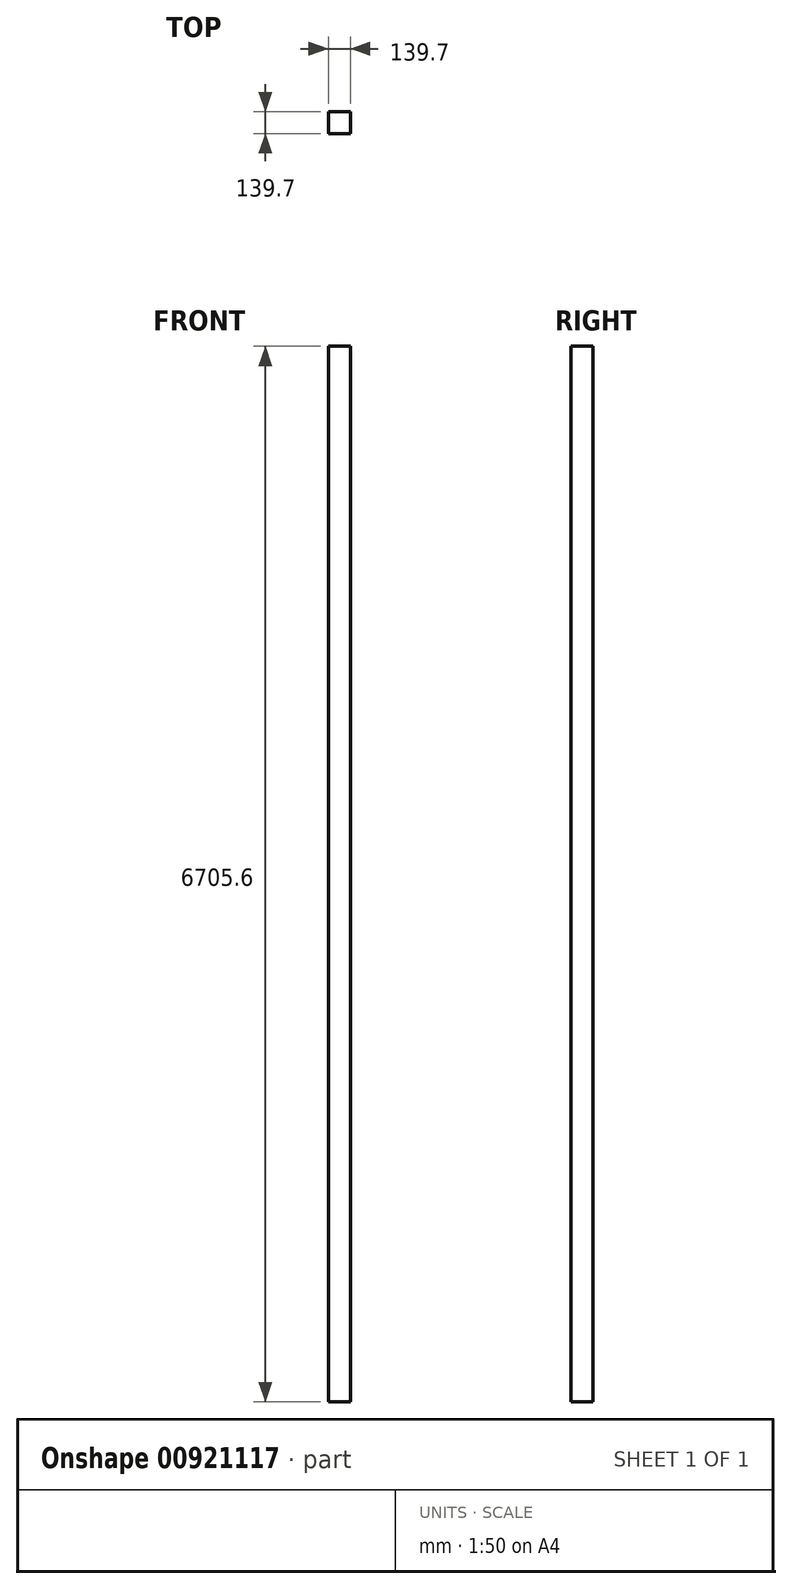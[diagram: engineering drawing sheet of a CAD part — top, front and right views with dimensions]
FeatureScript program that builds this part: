
annotation { "Feature Type Name" : "Feature", "Feature Type Description" : "" }
export const myFeature = defineFeature(function(context is Context, id is Id, definition is map)
    precondition{}
    {
        {
            var Q0;
            Q0=qCreatedBy(makeId("Top.planeOp"),FACE);
            var sketch = newSketch(context, id + "F0", { "sketchPlane" : qUnion([Q0])});
            skLineSegment(sketch, "E0.bottom", {"start": v(0, 40.07) * mm, "end": v(139.7, 40.07) * mm});
            skLineSegment(sketch, "E0.top", {"start": v(0, -99.63) * mm, "end": v(139.7, -99.63) * mm});
            skLineSegment(sketch, "E0.left", {"start": v(0, 40.07) * mm, "end": v(0, -99.63) * mm});
            skLineSegment(sketch, "E0.right", {"start": v(139.7, 40.07) * mm, "end": v(139.7, -99.63) * mm});
            skSolve(sketch);
        }
        {
            var Q0;
            Q0=qSketchRegion(id+"F0",true);
            extrude(context, id + "F1", {"entities" : qUnion([Q0]), "depth" : 22 * 304.8 * mm, "offsetDistance" : 25.4 * mm});
        }
        {
            var Q0;
            Q0=makeQuery(id+"F1.opExtrude","SWEPT_FACE",FACE,{"disambiguationData":[OSD([sQuery(id+"F0.wireOp",EDGE,"E0.right")])]});
            var sketch = newSketch(context, id + "F2", { "sketchPlane" : qUnion([Q0])});
            skLineSegment(sketch, "E1", {"start": v(-29.78, 6705.6) * mm, "end": v(-29.78, 6400.8) * mm, "construction": true});
            skLineSegment(sketch, "E2", {"start": v(-99.63, 6705.6) * mm, "end": v(40.07, 6705.6) * mm, "construction": true});
            skSolve(sketch);
        }
    });
